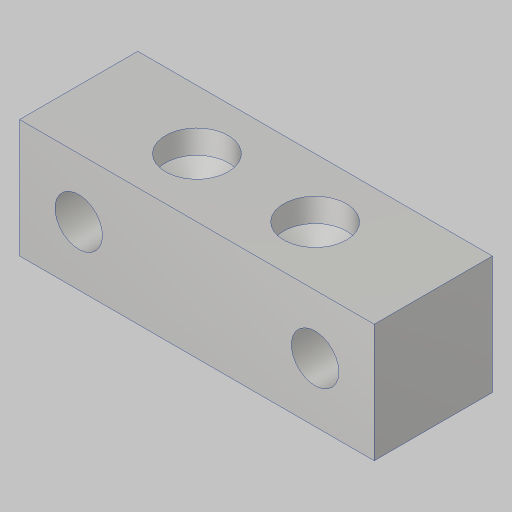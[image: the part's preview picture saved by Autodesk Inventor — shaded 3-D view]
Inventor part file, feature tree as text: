
AUTODESK INVENTOR PART (.ipt)
format: ipt  version: 2023.5 (Build 275446000, 446)  size: 126,464 bytes
history: native  units: in
note: dims shown in document units (in); Inventor stores cm internally (conversion verified against a paired STEP export)
features: sketch x3, hole x2, extrude x1
ambient origin geometry x8: Origin, YZ Plane, XZ Plane, XY Plane, X Axis, Y Axis, Z Axis, Center Point
bodies: Solid1 (feature_tree)
feature tree (6):
  extrude  "Extrusion1"  Depth=0.5in
  sketch  "Sketch2"  dims[d2=0.5in d3=0.0in d4=0.5in]
  hole  "Hole2"  [1 undecoded]
  hole  "Hole3"  [1 undecoded]
  sketch  "Sketch1"  dims[d0=1.5in d1=0.5in]
  sketch  "Sketch3"  dims[d12=1.0in d13=0.201in d14=0.38in d15=0.375in d16=0.25in d17=0.5635in d18=1.0in d19=0.8108in d20=0.25in d21=0.266in d22=0.75in d23=0.507in d24=0.25in d25=0.5635in d26=0.1in d27=0.8108in]
note: 2 required parameter values undecoded (feature->parameter linkage not recoverable at this tier; creation-order binding heuristic only, values carry confidence <= 0.55)
